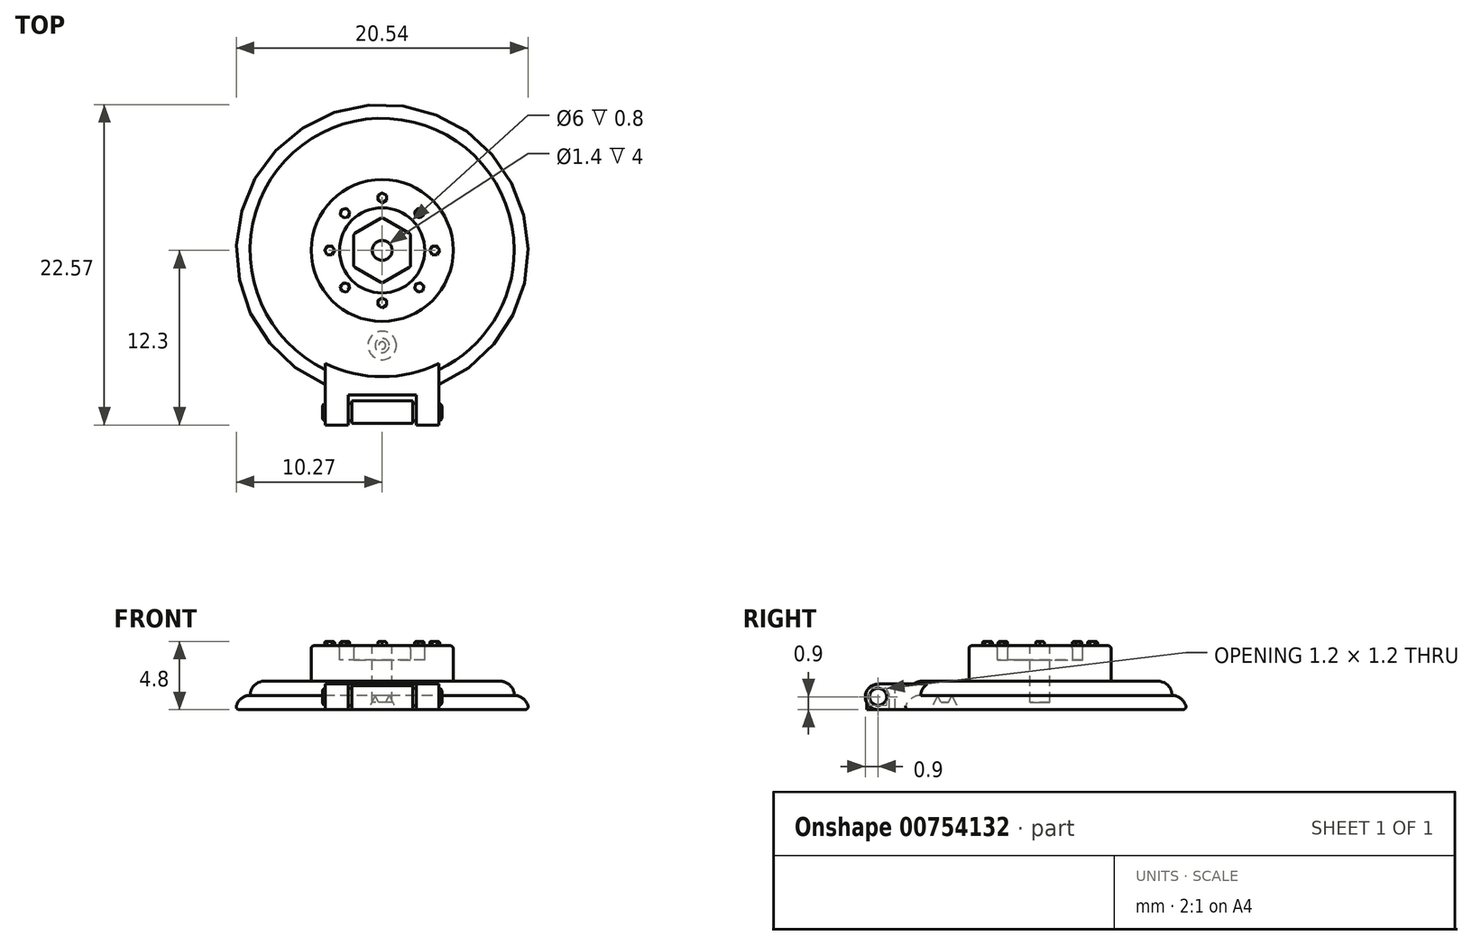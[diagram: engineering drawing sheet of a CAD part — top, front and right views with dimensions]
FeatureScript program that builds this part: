
annotation { "Feature Type Name" : "Feature", "Feature Type Description" : "" }
export const myFeature = defineFeature(function(context is Context, id is Id, definition is map)
    precondition{}
    {
        {
            var Q0;
            Q0=qCreatedBy(makeId("Right.planeOp"),FACE);
            var sketch = newSketch(context, id + "F0", { "sketchPlane" : qUnion([Q0])});
            skLineSegment(sketch, "E0", {"start": v(0, 0) * mm, "end": v(10.3, 0) * mm});
            skArc(sketch, "E1", {"start": v(10.3, 0) * mm, "mid": v(10, 0.7) * mm, "end": v(9.3, 1) * mm});
            skLineSegment(sketch, "E2", {"start": v(9.3, 1) * mm, "end": v(9.3, 1) * mm});
            skArc(sketch, "E3", {"start": v(9.3, 1) * mm, "mid": v(9, 1.7) * mm, "end": v(8.3, 2) * mm});
            skLineSegment(sketch, "E4", {"start": v(8.3, 2) * mm, "end": v(5, 2) * mm});
            skLineSegment(sketch, "E5", {"start": v(5, 2) * mm, "end": v(5, 4.5) * mm});
            skLineSegment(sketch, "E6", {"start": v(5, 4.5) * mm, "end": v(3, 4.5) * mm});
            skLineSegment(sketch, "E7", {"start": v(3, 4.5) * mm, "end": v(3, 3.5) * mm});
            skLineSegment(sketch, "E8", {"start": v(3, 3.5) * mm, "end": v(0, 3.5) * mm});
            skLineSegment(sketch, "E9", {"start": v(0, 3.5) * mm, "end": v(0, 0) * mm});
            skSolve(sketch);
        }
        {
            var Q0;
            Q0=makeQuery(id+"F0.imprint","IMPRINT",FACE,{"disambiguationData":[TD([[makeQuery(id+"F0.imprint","IMPRINT",EDGE,{"derivedFrom":sQuery(id+"F0.wireOp",EDGE,"E0")}),1.0]])]});
            var Q1;
            Q1=sQuery(id+"F0.wireOp",EDGE,"E9");
            revolve(context, id + "F1", {"surfaceOperationType" : NewSurfaceOperationType.NEW, "entities" : qUnion([Q0]), "axis" : qUnion([Q1]), "revolveType" : RevolveType.FULL});
        }
        {
            var Q0;
            Q0=makeQuery(id+"F1.opRevolve","SWEPT_FACE",FACE,{"disambiguationData":[OSD([sQuery(id+"F0.wireOp",EDGE,"E8")])]});
            var sketch = newSketch(context, id + "F2", { "sketchPlane" : qUnion([Q0])});
            skCircle(sketch, "E10.cCircle", {"center": v(0, 0) * mm, "radius": 2 * mm, "construction": true});
            skLineSegment(sketch, "E10.0", {"start": v(0, 2.3) * mm, "end": v(2, 1.15) * mm});
            skLineSegment(sketch, "E10.1", {"start": v(2, 1.15) * mm, "end": v(2, -1.15) * mm});
            skLineSegment(sketch, "E10.2", {"start": v(2, -1.15) * mm, "end": v(0, -2.3) * mm});
            skLineSegment(sketch, "E10.3", {"start": v(0, -2.3) * mm, "end": v(-2, -1.15) * mm});
            skLineSegment(sketch, "E10.4", {"start": v(-2, -1.15) * mm, "end": v(-2, 1.15) * mm});
            skLineSegment(sketch, "E10.5", {"start": v(-2, 1.15) * mm, "end": v(0, 2.3) * mm});
            skPoint(sketch, "E10.0.midPoint", {"position": v(1, 1.73) * mm});
            skSolve(sketch);
        }
        {
            var Q0;
            Q0=makeQuery(id+"F2.imprint","IMPRINT",FACE,{"disambiguationData":[TD([[makeQuery(id+"F2.imprint","IMPRINT",EDGE,{"derivedFrom":sQuery(id+"F2.wireOp",EDGE,"E10.0")}),-1.0]])]});
            extrude(context, id + "F3", {"entities" : qUnion([Q0]), "operationType" : NewBodyOperationType.ADD, "depth" : 1 * mm, "offsetDistance" : 25 * mm});
        }
        {
            var Q0;
            Q0=makeQuery(id+"F3.opExtrude","CAP_FACE",FACE,{"disambiguationData":[OSD([sQuery(id+"F2.wireOp",EDGE,"E10.0"),sQuery(id+"F2.wireOp",EDGE,"E10.1"),sQuery(id+"F2.wireOp",EDGE,"E10.2"),sQuery(id+"F2.wireOp",EDGE,"E10.3"),sQuery(id+"F2.wireOp",EDGE,"E10.4"),sQuery(id+"F2.wireOp",EDGE,"E10.5")])],"isStart":false});
            var Q1;
            Q1=makeQuery(id+"F1.opRevolve","SWEPT_FACE",FACE,{"disambiguationData":[OSD([sQuery(id+"F0.wireOp",EDGE,"E6")])]});
            var Q2;
            Q2=makeQuery(id+"F3.opExtrude","SWEPT_EDGE",EDGE,{"disambiguationData":[OSD([sQuery(id+"F2.wireOp",EDGE,"E10.2"),sQuery(id+"F2.wireOp",EDGE,"E10.3")])]});
            var Q3;
            Q3=makeQuery(id+"F3.opExtrude","SWEPT_EDGE",EDGE,{"disambiguationData":[OSD([sQuery(id+"F2.wireOp",EDGE,"E10.3"),sQuery(id+"F2.wireOp",EDGE,"E10.4")])]});
            var Q4;
            Q4=makeQuery(id+"F3.opExtrude","SWEPT_EDGE",EDGE,{"disambiguationData":[OSD([sQuery(id+"F2.wireOp",EDGE,"E10.1"),sQuery(id+"F2.wireOp",EDGE,"E10.2")])]});
            var Q5;
            Q5=makeQuery(id+"F3.opExtrude","SWEPT_EDGE",EDGE,{"disambiguationData":[OSD([sQuery(id+"F2.wireOp",EDGE,"E10.0"),sQuery(id+"F2.wireOp",EDGE,"E10.1")])]});
            var Q6;
            Q6=makeQuery(id+"F1.opRevolve","SWEPT_EDGE",EDGE,{"disambiguationData":[OSD([sQuery(id+"F0.wireOp",EDGE,"E0"),sQuery(id+"F0.wireOp",EDGE,"E1")])]});
            var Q7;
            Q7=makeQuery(id+"F3.opExtrude","SWEPT_EDGE",EDGE,{"disambiguationData":[OSD([sQuery(id+"F2.wireOp",EDGE,"E10.0"),sQuery(id+"F2.wireOp",EDGE,"E10.5")])]});
            var Q8;
            Q8=makeQuery(id+"F3.opExtrude","SWEPT_EDGE",EDGE,{"disambiguationData":[OSD([sQuery(id+"F2.wireOp",EDGE,"E10.4"),sQuery(id+"F2.wireOp",EDGE,"E10.5")])]});
            fillet(context, id + "F4", {"entities" : qUnion([Q0, Q1, Q2, Q3, Q4, Q5, Q6, Q7, Q8]), "radius" : 0.2 * mm, "tangentPropagation" : true, "allowEdgeOverflow" : false});
        }
        {
            var Q0;
            Q0=makeQuery(id+"F3.opExtrude","CAP_FACE",FACE,{"disambiguationData":[OSD([sQuery(id+"F2.wireOp",EDGE,"E10.0"),sQuery(id+"F2.wireOp",EDGE,"E10.1"),sQuery(id+"F2.wireOp",EDGE,"E10.2"),sQuery(id+"F2.wireOp",EDGE,"E10.3"),sQuery(id+"F2.wireOp",EDGE,"E10.4"),sQuery(id+"F2.wireOp",EDGE,"E10.5")])],"isStart":false});
            var sketch = newSketch(context, id + "F5", { "sketchPlane" : qUnion([Q0])});
            skCircle(sketch, "E11", {"center": v(0, 0) * mm, "radius": 0.7 * mm});
            skSolve(sketch);
        }
        {
            var Q0;
            Q0=makeQuery(id+"F5.imprint","IMPRINT",FACE,{"disambiguationData":[TD([[makeQuery(id+"F5.imprint","IMPRINT",EDGE,{"derivedFrom":sQuery(id+"F5.wireOp",EDGE,"E11")}),1.0]])]});
            extrude(context, id + "F6", {"entities" : qUnion([Q0]), "operationType" : NewBodyOperationType.REMOVE, "oppositeDirection" : true, "depth" : 4 * mm, "offsetDistance" : 25 * mm});
        }
        {
            var Q0;
            Q0=makeQuery(id+"F1.opRevolve","SWEPT_FACE",FACE,{"disambiguationData":[OSD([sQuery(id+"F0.wireOp",EDGE,"E6")])]});
            var sketch = newSketch(context, id + "F7", { "sketchPlane" : qUnion([Q0])});
            skCircle(sketch, "E12.cCircle", {"center": v(0, 3.7) * mm, "radius": 0.3 * mm});
            skLineSegment(sketch, "E12.0", {"start": v(0, 4.05) * mm, "end": v(0.3, 3.87) * mm});
            skLineSegment(sketch, "E12.1", {"start": v(0.3, 3.87) * mm, "end": v(0.3, 3.53) * mm});
            skLineSegment(sketch, "E12.2", {"start": v(0.3, 3.53) * mm, "end": v(0, 3.35) * mm});
            skLineSegment(sketch, "E12.3", {"start": v(0, 3.35) * mm, "end": v(-0.3, 3.53) * mm});
            skLineSegment(sketch, "E12.4", {"start": v(-0.3, 3.53) * mm, "end": v(-0.3, 3.87) * mm});
            skLineSegment(sketch, "E12.5", {"start": v(-0.3, 3.87) * mm, "end": v(0, 4.05) * mm});
            skPoint(sketch, "E12.0.midPoint", {"position": v(0.15, 3.96) * mm});
            skSolve(sketch);
        }
        {
            var Q0;
            {var subQ0=sQuery(id+"F7.wireOp",EDGE,"E12.4");var subQ1=sQuery(id+"F7.wireOp",EDGE,"E12.cCircle");var subQ2=makeQuery(id+"F7.imprint","INTERSECT",VERTEX,{"derivedFrom":[subQ1,subQ0]});Q0=makeQuery(id+"F7.imprint","IMPRINT",FACE,{"disambiguationData":[TD([[makeQuery(id+"F7.imprint","IMPRINT",EDGE,{"disambiguationData":[TD([[subQ2,-1.0]])],"derivedFrom":subQ1}),-1.0]])]});}
            var Q1;
            {var subQ0=sQuery(id+"F7.wireOp",EDGE,"E12.3");var subQ1=sQuery(id+"F7.wireOp",EDGE,"E12.cCircle");var subQ2=makeQuery(id+"F7.imprint","INTERSECT",VERTEX,{"derivedFrom":[subQ1,subQ0]});Q1=makeQuery(id+"F7.imprint","IMPRINT",FACE,{"disambiguationData":[TD([[makeQuery(id+"F7.imprint","IMPRINT",EDGE,{"disambiguationData":[TD([[subQ2,-1.0]])],"derivedFrom":subQ1}),-1.0]])]});}
            var Q2;
            {var subQ0=sQuery(id+"F7.wireOp",EDGE,"E12.1");var subQ1=sQuery(id+"F7.wireOp",EDGE,"E12.cCircle");var subQ2=makeQuery(id+"F7.imprint","INTERSECT",VERTEX,{"derivedFrom":[subQ1,subQ0]});Q2=makeQuery(id+"F7.imprint","IMPRINT",FACE,{"disambiguationData":[TD([[makeQuery(id+"F7.imprint","IMPRINT",EDGE,{"disambiguationData":[TD([[subQ2,1.0]])],"derivedFrom":subQ1}),-1.0]])]});}
            var Q3;
            {var subQ0=sQuery(id+"F7.wireOp",EDGE,"E12.5");var subQ1=sQuery(id+"F7.wireOp",EDGE,"E12.cCircle");var subQ2=makeQuery(id+"F7.imprint","INTERSECT",VERTEX,{"derivedFrom":[subQ1,subQ0]});Q3=makeQuery(id+"F7.imprint","IMPRINT",FACE,{"disambiguationData":[TD([[makeQuery(id+"F7.imprint","IMPRINT",EDGE,{"disambiguationData":[TD([[subQ2,-1.0]])],"derivedFrom":subQ1}),-1.0]])]});}
            var Q4;
            {var subQ0=sQuery(id+"F7.wireOp",EDGE,"E12.0");var subQ1=sQuery(id+"F7.wireOp",EDGE,"E12.cCircle");var subQ2=makeQuery(id+"F7.imprint","INTERSECT",VERTEX,{"derivedFrom":[subQ1,subQ0]});Q4=makeQuery(id+"F7.imprint","IMPRINT",FACE,{"disambiguationData":[TD([[makeQuery(id+"F7.imprint","IMPRINT",EDGE,{"disambiguationData":[TD([[subQ2,-1.0]])],"derivedFrom":subQ1}),-1.0]])]});}
            var Q5;
            {var subQ0=sQuery(id+"F7.wireOp",EDGE,"E12.0");var subQ1=sQuery(id+"F7.wireOp",EDGE,"E12.cCircle");var subQ2=makeQuery(id+"F7.imprint","INTERSECT",VERTEX,{"derivedFrom":[subQ1,subQ0]});Q5=makeQuery(id+"F7.imprint","IMPRINT",FACE,{"disambiguationData":[TD([[makeQuery(id+"F7.imprint","IMPRINT",EDGE,{"disambiguationData":[TD([[subQ2,1.0]])],"derivedFrom":subQ1}),-1.0]])]});}
            var Q6;
            {var subQ0=sQuery(id+"F7.wireOp",EDGE,"E12.cCircle");var subQ4=makeQuery(id+"F7.imprint","INTERSECT",VERTEX,{"derivedFrom":[subQ0,sQuery(id+"F7.wireOp",EDGE,"E12.0")]});Q6=makeQuery(id+"F7.imprint","IMPRINT",FACE,{"disambiguationData":[TD([[makeQuery(id+"F7.imprint","IMPRINT",EDGE,{"disambiguationData":[TD([[subQ4,1.0]])],"derivedFrom":subQ0}),1.0]])]});}
            var Q7;
            Q7=sQuery(id+"F7.wireOp",EDGE,"E12.4");
            var Q8;
            Q8=sQuery(id+"F7.wireOp",EDGE,"E12.3");
            var Q9;
            Q9=sQuery(id+"F7.wireOp",EDGE,"E12.2");
            var Q10;
            Q10=sQuery(id+"F7.wireOp",EDGE,"E12.1");
            var Q11;
            Q11=sQuery(id+"F7.wireOp",EDGE,"E12.0");
            var Q12;
            Q12=sQuery(id+"F7.wireOp",EDGE,"E12.5");
            extrude(context, id + "F8", {"entities" : qUnion([Q0, Q1, Q2, Q3, Q4, Q5, Q6]), "surfaceEntities" : qUnion([Q7, Q8, Q9, Q10, Q11, Q12]), "depth" : 0.3 * mm, "offsetDistance" : 25 * mm});
        }
        {
            var Q0;
            Q0=makeQuery(id+"F8.opExtrude","SWEPT_BODY",BODY,{"disambiguationData":[OSD([sQuery(id+"F7.wireOp",EDGE,"E12.0"),sQuery(id+"F7.wireOp",EDGE,"E12.1"),sQuery(id+"F7.wireOp",EDGE,"E12.2"),sQuery(id+"F7.wireOp",EDGE,"E12.3"),sQuery(id+"F7.wireOp",EDGE,"E12.4"),sQuery(id+"F7.wireOp",EDGE,"E12.5")])]});
            var Q1;
            {var subQ0=sQuery(id+"F0.wireOp",EDGE,"E6");Q1=makeQuery(id+"F4.opFillet","BLEND_EDGE",EDGE,{"blendedFrom":[makeQuery(id+"F1.opRevolve","SWEPT_EDGE",EDGE,{"disambiguationData":[OSD([subQ0,sQuery(id+"F0.wireOp",EDGE,"E7")])]}),makeQuery(id+"F1.opRevolve","SWEPT_FACE",FACE,{"disambiguationData":[OSD([subQ0])]})],"blendedInto":[makeQuery(id+"F1.opRevolve","SWEPT_FACE",FACE,{"disambiguationData":[OSD([subQ0])]})]});}
            circularPattern(context, id + "F9", {"operationType" : NewBodyOperationType.ADD, "entities" : qUnion([Q0]), "axis" : qUnion([Q1]), "angle" : 360 * degree, "instanceCount" : 8, "equalSpace" : true});
        }
        {
            var Q0;
            Q0=qCreatedBy(makeId("Right.planeOp"),FACE);
            var sketch = newSketch(context, id + "F10", { "sketchPlane" : qUnion([Q0])});
            skLineSegment(sketch, "E13", {"start": v(-4, 0) * mm, "end": v(-11.4, 0) * mm});
            skArc(sketch, "E14", {"start": v(-11.4, 1.8) * mm, "mid": v(-12.3, 0.9) * mm, "end": v(-11.4, 0) * mm});
            skLineSegment(sketch, "E15", {"start": v(-11.4, 1.8) * mm, "end": v(-4, 1.8) * mm});
            skLineSegment(sketch, "E16", {"start": v(-4, 1.8) * mm, "end": v(-4, 0) * mm});
            skArc(sketch, "E17", {"start": v(-11.4, 0) * mm, "mid": v(-10.5, 0.9) * mm, "end": v(-11.4, 1.8) * mm, "construction": true});
            skSolve(sketch);
        }
        {
            var Q0;
            Q0=makeQuery(id+"F10.imprint","IMPRINT",FACE,{"disambiguationData":[TD([[makeQuery(id+"F10.imprint","IMPRINT",EDGE,{"derivedFrom":sQuery(id+"F10.wireOp",EDGE,"E13")}),-1.0]])]});
            extrude(context, id + "F11", {"entities" : qUnion([Q0]), "operationType" : NewBodyOperationType.ADD, "endBound" : BoundingType.SYMMETRIC, "depth" : 8 * mm, "offsetDistance" : 25 * mm});
        }
        {
            var Q0;
            Q0=makeQuery(id+"F11.opExtrude","SWEPT_FACE",FACE,{"disambiguationData":[OSD([sQuery(id+"F10.wireOp",EDGE,"E15")])]});
            var sketch = newSketch(context, id + "F12", { "sketchPlane" : qUnion([Q0])});
            skLineSegment(sketch, "E18.bottom", {"start": v(-2.4, -10.2) * mm, "end": v(2.4, -10.2) * mm});
            skLineSegment(sketch, "E18.top", {"start": v(-2.4, -15.2) * mm, "end": v(2.4, -15.2) * mm});
            skLineSegment(sketch, "E18.left", {"start": v(-2.4, -10.2) * mm, "end": v(-2.4, -15.2) * mm});
            skLineSegment(sketch, "E18.right", {"start": v(2.4, -10.2) * mm, "end": v(2.4, -15.2) * mm});
            skSolve(sketch);
        }
        {
            var Q0;
            {var subQ0=sQuery(id+"F12.wireOp",EDGE,"E18.bottom");Q0=makeQuery(id+"F12.imprint","IMPRINT",FACE,{"disambiguationData":[TD([[makeQuery(id+"F12.imprint","IMPRINT",EDGE,{"derivedFrom":subQ0}),-1.0]])]});}
            var Q1;
            {var subQ0=sQuery(id+"F12.wireOp",EDGE,"E18.top");Q1=makeQuery(id+"F12.imprint","IMPRINT",FACE,{"disambiguationData":[TD([[makeQuery(id+"F12.imprint","IMPRINT",EDGE,{"derivedFrom":subQ0}),1.0]])]});}
            extrude(context, id + "F13", {"entities" : qUnion([Q0, Q1]), "operationType" : NewBodyOperationType.REMOVE, "endBound" : BoundingType.THROUGH_ALL, "oppositeDirection" : true, "depth" : 25 * mm, "offsetDistance" : 25 * mm});
        }
        {
            var Q0;
            Q0=qCreatedBy(makeId("Right.planeOp"),FACE);
            var sketch = newSketch(context, id + "F14", { "sketchPlane" : qUnion([Q0])});
            skCircle(sketch, "E19", {"center": v(-11.4, 0.9) * mm, "radius": 0.6 * mm});
            skSolve(sketch);
        }
        {
            var Q0;
            Q0=makeQuery(id+"F14.imprint","IMPRINT",FACE,{"disambiguationData":[TD([[makeQuery(id+"F14.imprint","IMPRINT",EDGE,{"derivedFrom":sQuery(id+"F14.wireOp",EDGE,"E19")}),1.0]])]});
            extrude(context, id + "F15", {"entities" : qUnion([Q0]), "operationType" : NewBodyOperationType.ADD, "endBound" : BoundingType.SYMMETRIC, "depth" : 8.4 * mm, "offsetDistance" : 25 * mm});
        }
        {
            var Q0;
            Q0=makeQuery(id+"F15.opExtrude","CAP_FACE",FACE,{"disambiguationData":[OSD([sQuery(id+"F14.wireOp",EDGE,"E19")])],"isStart":false});
            var Q1;
            Q1=makeQuery(id+"F15.opExtrude","CAP_FACE",FACE,{"disambiguationData":[OSD([sQuery(id+"F14.wireOp",EDGE,"E19")])],"isStart":true});
            fillet(context, id + "F16", {"entities" : qUnion([Q0, Q1]), "radius" : 0.2 * mm, "tangentPropagation" : true, "allowEdgeOverflow" : false});
        }
        {
            var Q0;
            Q0=qCreatedBy(makeId("Right.planeOp"),FACE);
            var sketch = newSketch(context, id + "F17", { "sketchPlane" : qUnion([Q0])});
            skArc(sketch, "E20", {"start": v(-10.6, 0.9) * mm, "mid": v(-11.4, 1.7) * mm, "end": v(-12.2, 0.9) * mm});
            skLineSegment(sketch, "E21", {"start": v(-12.2, 0.9) * mm, "end": v(-12.2, 0) * mm});
            skLineSegment(sketch, "E22", {"start": v(-12.2, 0) * mm, "end": v(-10.6, 0) * mm});
            skLineSegment(sketch, "E23", {"start": v(-10.6, 0) * mm, "end": v(-10.6, 0.9) * mm});
            skSolve(sketch);
        }
        {
            var Q0;
            Q0=makeQuery(id+"F17.imprint","IMPRINT",FACE,{"disambiguationData":[TD([[makeQuery(id+"F17.imprint","IMPRINT",EDGE,{"derivedFrom":sQuery(id+"F17.wireOp",EDGE,"E20")}),1.0]])]});
            extrude(context, id + "F18", {"entities" : qUnion([Q0]), "operationType" : NewBodyOperationType.ADD, "endBound" : BoundingType.SYMMETRIC, "depth" : 4.3 * mm, "offsetDistance" : 25 * mm});
        }
        {
            var Q0;
            Q0=makeQuery(id+"F9.opPattern","COPY",FACE,{"derivedFrom":makeQuery(id+"F8.opExtrude","CAP_FACE",FACE,{"disambiguationData":[OSD([sQuery(id+"F7.wireOp",EDGE,"E12.0"),sQuery(id+"F7.wireOp",EDGE,"E12.1"),sQuery(id+"F7.wireOp",EDGE,"E12.2"),sQuery(id+"F7.wireOp",EDGE,"E12.3"),sQuery(id+"F7.wireOp",EDGE,"E12.4"),sQuery(id+"F7.wireOp",EDGE,"E12.5")])],"isStart":false}),"instanceName":"7"});
            var Q1;
            Q1=makeQuery(id+"F9.opPattern","COPY",FACE,{"derivedFrom":makeQuery(id+"F8.opExtrude","CAP_FACE",FACE,{"disambiguationData":[OSD([sQuery(id+"F7.wireOp",EDGE,"E12.0"),sQuery(id+"F7.wireOp",EDGE,"E12.1"),sQuery(id+"F7.wireOp",EDGE,"E12.2"),sQuery(id+"F7.wireOp",EDGE,"E12.3"),sQuery(id+"F7.wireOp",EDGE,"E12.4"),sQuery(id+"F7.wireOp",EDGE,"E12.5")])],"isStart":false}),"instanceName":"6"});
            var Q2;
            Q2=makeQuery(id+"F9.opPattern","COPY",FACE,{"derivedFrom":makeQuery(id+"F8.opExtrude","CAP_FACE",FACE,{"disambiguationData":[OSD([sQuery(id+"F7.wireOp",EDGE,"E12.0"),sQuery(id+"F7.wireOp",EDGE,"E12.1"),sQuery(id+"F7.wireOp",EDGE,"E12.2"),sQuery(id+"F7.wireOp",EDGE,"E12.3"),sQuery(id+"F7.wireOp",EDGE,"E12.4"),sQuery(id+"F7.wireOp",EDGE,"E12.5")])],"isStart":false}),"instanceName":"5"});
            var Q3;
            Q3=makeQuery(id+"F9.opPattern","COPY",FACE,{"derivedFrom":makeQuery(id+"F8.opExtrude","CAP_FACE",FACE,{"disambiguationData":[OSD([sQuery(id+"F7.wireOp",EDGE,"E12.0"),sQuery(id+"F7.wireOp",EDGE,"E12.1"),sQuery(id+"F7.wireOp",EDGE,"E12.2"),sQuery(id+"F7.wireOp",EDGE,"E12.3"),sQuery(id+"F7.wireOp",EDGE,"E12.4"),sQuery(id+"F7.wireOp",EDGE,"E12.5")])],"isStart":false}),"instanceName":"4"});
            var Q4;
            Q4=makeQuery(id+"F9.opPattern","COPY",FACE,{"derivedFrom":makeQuery(id+"F8.opExtrude","CAP_FACE",FACE,{"disambiguationData":[OSD([sQuery(id+"F7.wireOp",EDGE,"E12.0"),sQuery(id+"F7.wireOp",EDGE,"E12.1"),sQuery(id+"F7.wireOp",EDGE,"E12.2"),sQuery(id+"F7.wireOp",EDGE,"E12.3"),sQuery(id+"F7.wireOp",EDGE,"E12.4"),sQuery(id+"F7.wireOp",EDGE,"E12.5")])],"isStart":false}),"instanceName":"3"});
            var Q5;
            Q5=makeQuery(id+"F9.opPattern","COPY",FACE,{"derivedFrom":makeQuery(id+"F8.opExtrude","CAP_FACE",FACE,{"disambiguationData":[OSD([sQuery(id+"F7.wireOp",EDGE,"E12.0"),sQuery(id+"F7.wireOp",EDGE,"E12.1"),sQuery(id+"F7.wireOp",EDGE,"E12.2"),sQuery(id+"F7.wireOp",EDGE,"E12.3"),sQuery(id+"F7.wireOp",EDGE,"E12.4"),sQuery(id+"F7.wireOp",EDGE,"E12.5")])],"isStart":false}),"instanceName":"2"});
            var Q6;
            Q6=makeQuery(id+"F9.opPattern","COPY",FACE,{"derivedFrom":makeQuery(id+"F8.opExtrude","CAP_FACE",FACE,{"disambiguationData":[OSD([sQuery(id+"F7.wireOp",EDGE,"E12.0"),sQuery(id+"F7.wireOp",EDGE,"E12.1"),sQuery(id+"F7.wireOp",EDGE,"E12.2"),sQuery(id+"F7.wireOp",EDGE,"E12.3"),sQuery(id+"F7.wireOp",EDGE,"E12.4"),sQuery(id+"F7.wireOp",EDGE,"E12.5")])],"isStart":false}),"instanceName":"1"});
            var Q7;
            Q7=makeQuery(id+"F8.opExtrude","CAP_FACE",FACE,{"disambiguationData":[OSD([sQuery(id+"F7.wireOp",EDGE,"E12.0"),sQuery(id+"F7.wireOp",EDGE,"E12.1"),sQuery(id+"F7.wireOp",EDGE,"E12.2"),sQuery(id+"F7.wireOp",EDGE,"E12.3"),sQuery(id+"F7.wireOp",EDGE,"E12.4"),sQuery(id+"F7.wireOp",EDGE,"E12.5")])],"isStart":false});
            fillet(context, id + "F19", {"entities" : qUnion([Q0, Q1, Q2, Q3, Q4, Q5, Q6, Q7]), "radius" : 0.1 * mm, "tangentPropagation" : true, "allowEdgeOverflow" : false});
        }
        {
            var Q0;
            Q0=qCreatedBy(makeId("Right.planeOp"),FACE);
            var sketch = newSketch(context, id + "F20", { "sketchPlane" : qUnion([Q0])});
            skLineSegment(sketch, "E24", {"start": v(0, 4.5) * mm, "end": v(0, -0.5) * mm});
            skLineSegment(sketch, "E25", {"start": v(-2.08, 4.5) * mm, "end": v(2.08, 4.5) * mm, "construction": true});
            skLineSegment(sketch, "E26", {"start": v(-6.7, 0) * mm, "end": v(-6.7, 0.5) * mm});
            skLineSegment(sketch, "E27", {"start": v(-6.7, 0.5) * mm, "end": v(-6.45, 0.5) * mm});
            skLineSegment(sketch, "E28", {"start": v(-6.45, 0.5) * mm, "end": v(-6.2, 1) * mm});
            skLineSegment(sketch, "E29", {"start": v(-6.2, 1) * mm, "end": v(-5.7, 0) * mm});
            skLineSegment(sketch, "E30", {"start": v(-5.7, 0) * mm, "end": v(-6.7, 0) * mm});
            skSolve(sketch);
        }
        {
            var Q0;
            Q0 = qSketchRegion(id + "F20", true);
            var Q1;
            Q1=sQuery(id+"F20.wireOp",EDGE,"E26");
            revolve(context, id + "F21", {"operationType" : NewBodyOperationType.REMOVE, "surfaceOperationType" : NewSurfaceOperationType.NEW, "entities" : qUnion([Q0]), "axis" : qUnion([Q1]), "revolveType" : RevolveType.FULL, "oppositeDirection" : true});
        }
    });
